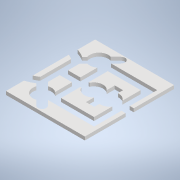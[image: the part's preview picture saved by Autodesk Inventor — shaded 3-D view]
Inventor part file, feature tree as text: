
AUTODESK INVENTOR PART (.ipt)
format: ipt  version: 2021 (Build 250183000, 183)  size: 209,408 bytes
history: native  units: mm
features: other x8, reference x7, extrude x1, sketch x1
ambient origin geometry x8: Origin, YZ Plane, XZ Plane, XY Plane, X Axis, Y Axis, Z Axis, Center Point
bodies: Body1 (feature_tree)
feature tree (17):
  other  "Sólido1"
  extrude  "Extrusión1"  Depth=10.0mm
  sketch  "Boceto1"  dims[d1=2.0mm d3=2.0mm d4=2.0mm d5=2.0mm d6=10.0mm d7=0.0mm]
  reference  "Referencia2"
  reference  "Referencia3"
  reference  "Referencia4"
  reference  "Referencia5"
  reference  "Referencia6"
  reference  "Referencia7"
  reference  "Referencia8"
  other  "<userpath>\OneDrive\Robotica\Proyecto-Rob\Piezas\Ensamble1.iam"
  other  "Ensamble1.iam"
  other  "Etapa2Base:1"
  other  "T:1"
  other  "Pinzas:1"
  other  "Pinzas:2"
  other  "BaseGripper:1"
